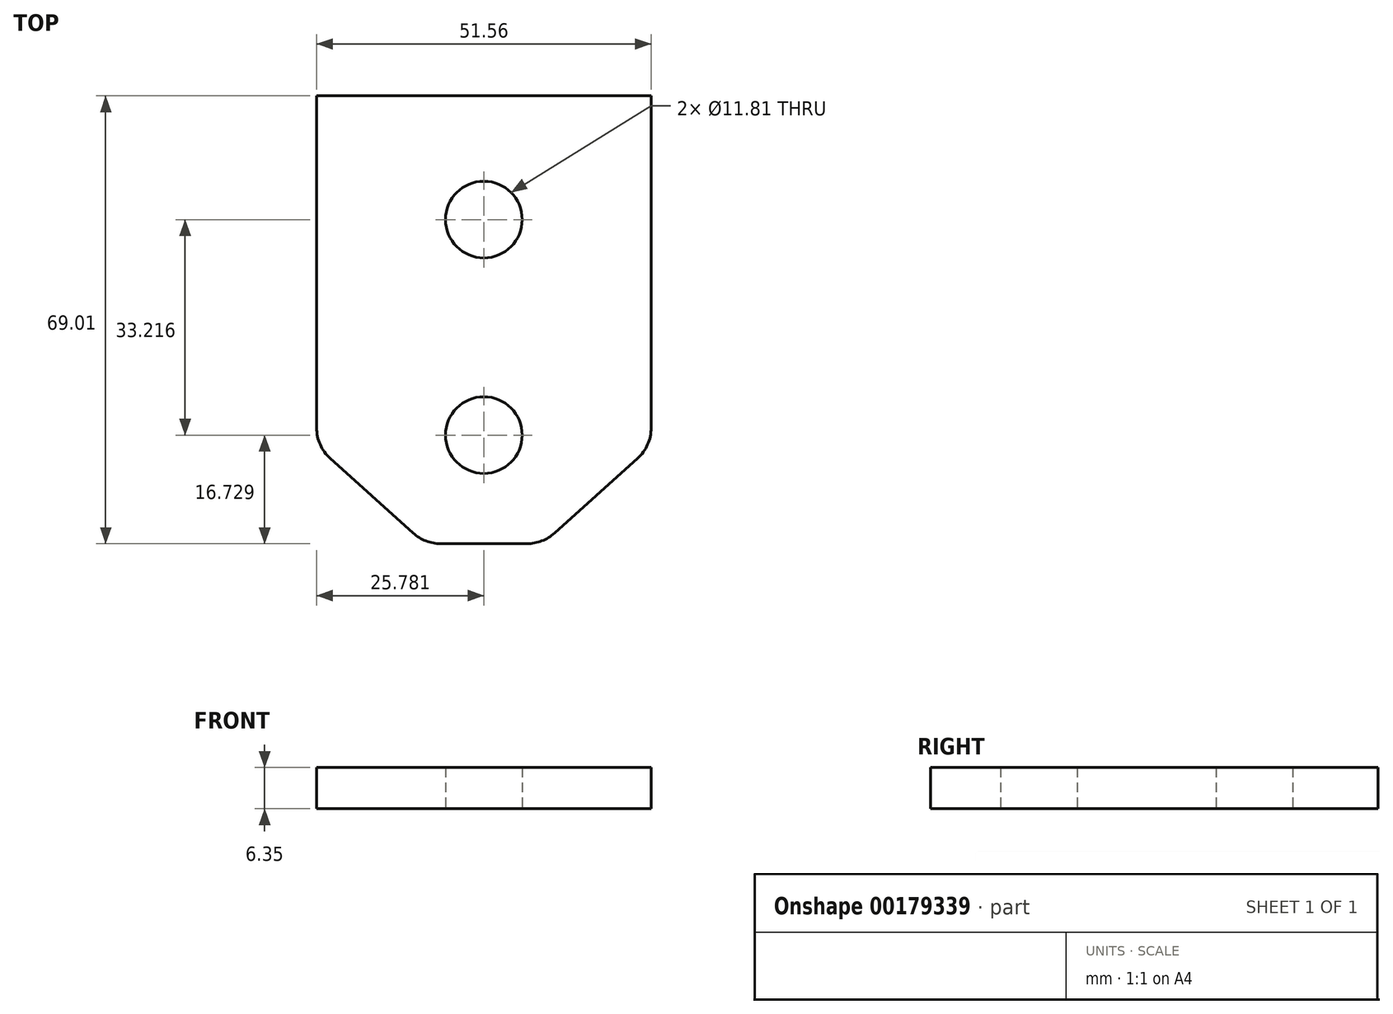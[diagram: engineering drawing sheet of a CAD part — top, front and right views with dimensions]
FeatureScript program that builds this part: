
annotation { "Feature Type Name" : "Feature", "Feature Type Description" : "" }
export const myFeature = defineFeature(function(context is Context, id is Id, definition is map)
    precondition{}
    {
        {
            var Q0;
            Q0=qCreatedBy(makeId("Top.planeOp"),FACE);
            var sketch = newSketch(context, id + "F0", { "sketchPlane" : qUnion([Q0])});
            skLineSegment(sketch, "E0", {"start": v(25.78, 69) * mm, "end": v(0, 69) * mm});
            skPoint(sketch, "E1.orphan", {"position": v(25.78, 69) * mm});
            skPoint(sketch, "E2.visualSharp", {"position": v(51.56, -39.2) * mm});
            skArc(sketch, "E3", {"start": v(25.78, 55.85) * mm, "mid": v(19.88, 49.95) * mm, "end": v(25.78, 44.04) * mm});
            skArc(sketch, "E4", {"start": v(25.78, 22.63) * mm, "mid": v(19.88, 16.73) * mm, "end": v(25.78, 10.82) * mm});
            skLineSegment(sketch, "E5", {"start": v(0, 69) * mm, "end": v(0, 17.86) * mm});
            skLineSegment(sketch, "E6", {"start": v(2.1, 13.14) * mm, "end": v(9.17, 6.78) * mm});
            skPoint(sketch, "E7.visualSharp", {"position": v(51.56, -31.4) * mm});
            skPoint(sketch, "E8.start.orphan", {"position": v(51.56, 69) * mm});
            skLineSegment(sketch, "E9.MirrorCS", {"start": v(25.78, 69) * mm, "end": v(51.56, 69) * mm});
            skLineSegment(sketch, "E10.MirrorCS", {"start": v(51.56, 69) * mm, "end": v(51.56, 17.86) * mm});
            skArc(sketch, "E11.MirrorCS", {"start": v(25.78, 55.85) * mm, "mid": v(31.69, 49.95) * mm, "end": v(25.78, 44.04) * mm});
            skArc(sketch, "E12.MirrorCS", {"start": v(25.78, 22.63) * mm, "mid": v(31.69, 16.73) * mm, "end": v(25.78, 10.82) * mm});
            skLineSegment(sketch, "E13.MirrorCS", {"start": v(49.46, 13.14) * mm, "end": v(42.4, 6.78) * mm});
            skPoint(sketch, "E14.visualSharp", {"position": v(0, 15.03) * mm});
            skArc(sketch, "E14.filletArc", {"start": v(0, 17.86) * mm, "mid": v(0.55, 15.28) * mm, "end": v(2.1, 13.14) * mm});
            skPoint(sketch, "E15.visualSharp", {"position": v(51.56, 15.03) * mm});
            skArc(sketch, "E15.filletArc", {"start": v(49.46, 13.14) * mm, "mid": v(51.01, 15.28) * mm, "end": v(51.56, 17.86) * mm});
            skLineSegment(sketch, "E16", {"start": v(49.46, 13.14) * mm, "end": v(36.68, 1.63) * mm});
            skLineSegment(sketch, "E17", {"start": v(2.1, 13.14) * mm, "end": v(14.88, 1.63) * mm});
            skLineSegment(sketch, "E18", {"start": v(19.13, 0) * mm, "end": v(32.43, 0) * mm});
            skPoint(sketch, "E19.visualSharp", {"position": v(16.7, 0) * mm});
            skArc(sketch, "E19.filletArc", {"start": v(14.88, 1.63) * mm, "mid": v(16.86, 0.42) * mm, "end": v(19.13, 0) * mm});
            skPoint(sketch, "E20.visualSharp", {"position": v(34.87, 0) * mm});
            skArc(sketch, "E20.filletArc", {"start": v(32.43, 0) * mm, "mid": v(34.7, 0.42) * mm, "end": v(36.68, 1.63) * mm});
            skSolve(sketch);
        }
        {
            var Q0;
            Q0=makeQuery(id+"F0.imprint","IMPRINT",FACE,{"disambiguationData":[TD([[makeQuery(id+"F0.imprint","IMPRINT",EDGE,{"derivedFrom":sQuery(id+"F0.wireOp",EDGE,"E0")}),1.0]])]});
            extrude(context, id + "F1", {"entities" : qUnion([Q0]), "depth" : 6.35 * mm});
        }
    });
